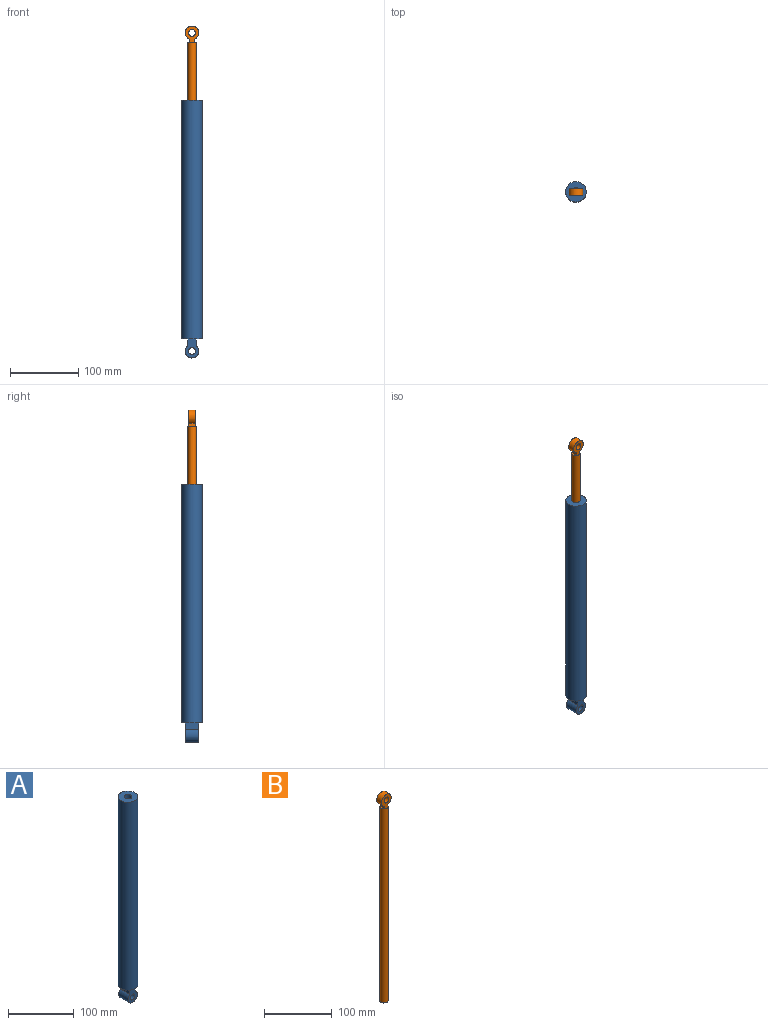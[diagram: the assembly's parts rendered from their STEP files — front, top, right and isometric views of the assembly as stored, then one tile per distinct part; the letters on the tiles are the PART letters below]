
ASSEMBLY  parts=2 mates=1
PART A: 11 faces, bbox 30x30x378 mm
  f0: plane 30x30mm, normal (0,0,-1), area 466.9mm2, adj f2,f3,f5,f7,f8
  f1: plane 30x30mm, normal (0,0,1), area 593.8mm2, adj f2,f9
  f2: cylinder r=15mm len=350mm, axis (0,0,1), area 32986.7mm2, adj f0,f1
  f3: plane 20x10mm, normal (-1,0,0), area 200mm2, adj f0,f4,f7,f8
  f4: cylinder r=10mm len=20mm, axis (0,1,0), area 999.2mm2, adj f3,f5,f7,f8
  f5: plane 20x10mm, normal (1,0,0), area 200mm2, adj f0,f4,f7,f8
  f6: cylinder r=5mm len=20mm, axis (0,1,0), area 628.3mm2, adj f7,f8
  f7: plane 28x20mm, normal (0,-1,0), area 339.3mm2, adj f0,f3,f4,f5,f6
  f8: plane 28x20mm, normal (0,1,0), area 339.3mm2, adj f0,f3,f4,f5,f6
  f9: cylinder r=6mm len=180mm, axis (0,0,1), area 6785.8mm2, adj f1,f10
  f10: plane 12x12mm, normal (0,0,1), area 113.1mm2, adj f9
PART B: 9 faces, bbox 20x12x374.5 mm
  f0: plane 12x12mm, normal (0,0,1), area 53.1mm2, adj f2,f3,f5,f7,f8
  f1: plane 12x12mm, normal (0,0,-1), area 113.1mm2, adj f2
  f2: cylinder r=6mm len=350mm, axis (0,0,-1), area 13194.7mm2, adj f0,f1
  f3: plane 10x5mm, normal (1,0,0), area 50mm2, adj f0,f4,f7,f8
  f4: cylinder r=10mm len=20mm, axis (0,1,0), area 567.4mm2, adj f3,f5,f7,f8
  f5: plane 10x5mm, normal (-1,0,0), area 50mm2, adj f0,f4,f7,f8
  f6: cylinder r=5mm len=10mm, axis (0,1,0), area 314.2mm2, adj f7,f8
  f7: plane 24.54x20mm, normal (0,-1,0), area 263.8mm2, adj f0,f3,f4,f5,f6
  f8: plane 24.54x20mm, normal (0,1,0), area 263.8mm2, adj f0,f3,f4,f5,f6
PLACE A rot(axis=(0,0,-1),0deg) t=(19.43,-131.57,-57.17)mm fixed
PLACE B rot(axis=(0,0,-1),0deg) t=(19.43,-131.57,-323.13)mm
MATE slider A.f2 <-> B.f2  axis (0,0,1) through (19.43,-131.57,-57.17)mm
